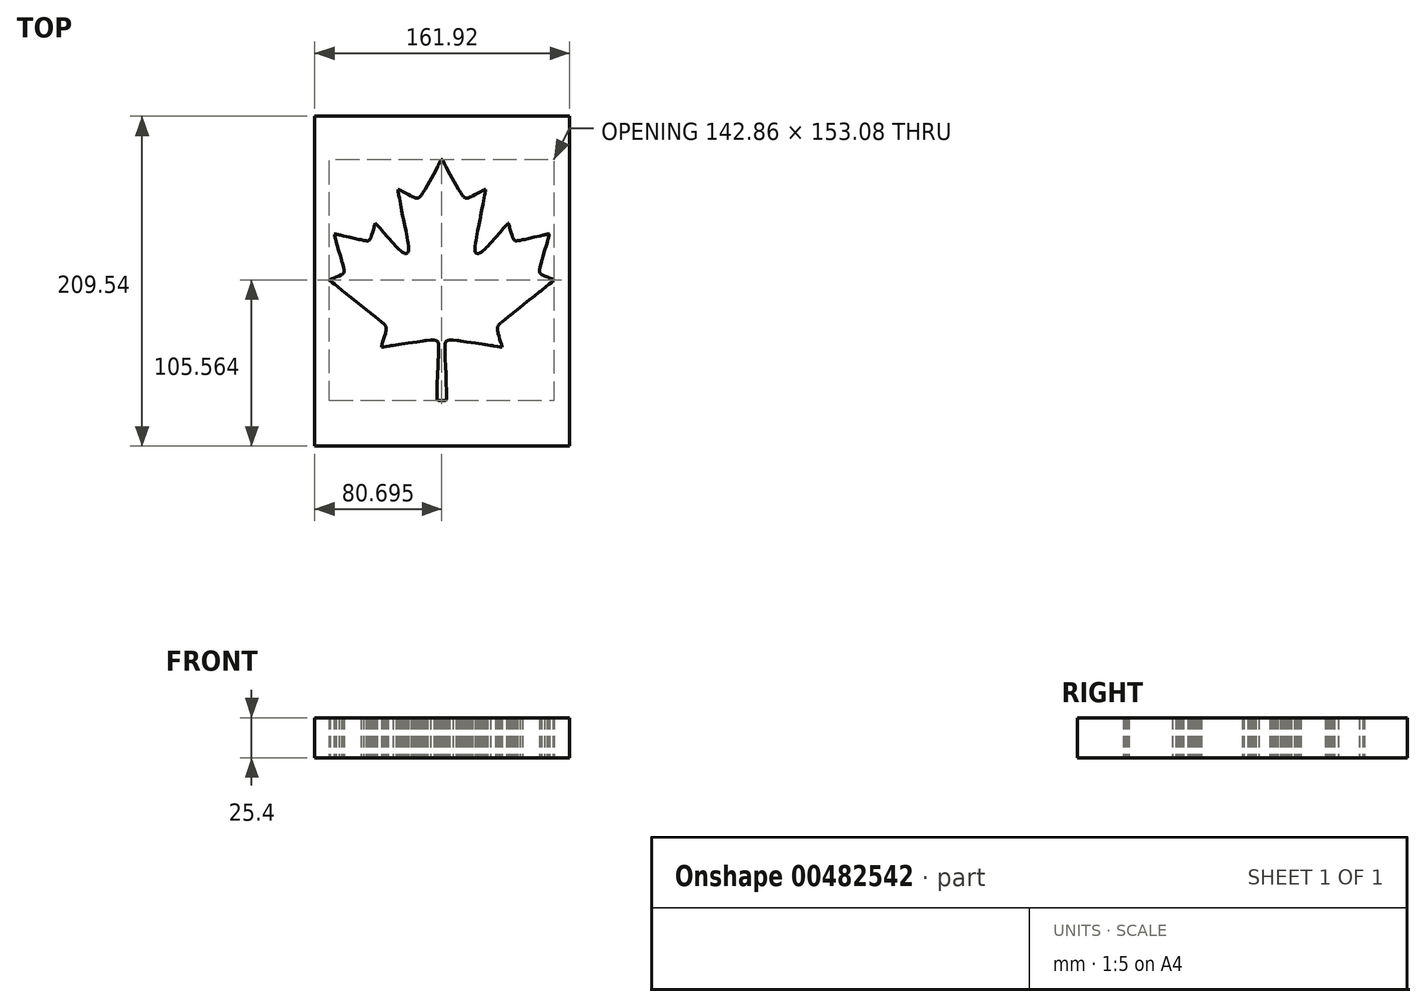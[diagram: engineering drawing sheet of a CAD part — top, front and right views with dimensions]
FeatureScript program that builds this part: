
annotation { "Feature Type Name" : "Feature", "Feature Type Description" : "" }
export const myFeature = defineFeature(function(context is Context, id is Id, definition is map)
    precondition{}
    {
        {
            var Q0;
            Q0=qCreatedBy(makeId("Top.planeOp"),FACE);
            var sketch = newSketch(context, id + "F0", { "sketchPlane" : qUnion([Q0])});
            skLineSegment(sketch, "E0", {"start": v(-80.96, -104.78) * mm, "end": v(80.96, -104.78) * mm});
            skLineSegment(sketch, "E1", {"start": v(80.96, -104.78) * mm, "end": v(80.96, 104.78) * mm});
            skLineSegment(sketch, "E2", {"start": v(80.96, 104.78) * mm, "end": v(-80.96, 104.78) * mm});
            skLineSegment(sketch, "E3", {"start": v(-80.96, 104.78) * mm, "end": v(-80.96, -104.78) * mm});
            skLineSegment(sketch, "E4", {"start": v(-2.37, 73.77) * mm, "end": v(-2.87, 72.84) * mm});
            skLineSegment(sketch, "E5", {"start": v(-2.87, 72.84) * mm, "end": v(-4.36, 70.05) * mm});
            skLineSegment(sketch, "E6", {"start": v(-4.36, 70.05) * mm, "end": v(-6.8, 65.54) * mm});
            skLineSegment(sketch, "E7", {"start": v(-6.8, 65.54) * mm, "end": v(-9.3, 61.02) * mm});
            skLineSegment(sketch, "E8", {"start": v(-9.3, 61.02) * mm, "end": v(-10.93, 58.16) * mm});
            skLineSegment(sketch, "E9", {"start": v(-10.93, 58.16) * mm, "end": v(-11.5, 57.22) * mm});
            skLineSegment(sketch, "E10", {"start": v(-11.5, 57.22) * mm, "end": v(-11.71, 56.87) * mm});
            skLineSegment(sketch, "E11", {"start": v(-11.71, 56.87) * mm, "end": v(-12.38, 55.81) * mm});
            skLineSegment(sketch, "E12", {"start": v(-12.38, 55.81) * mm, "end": v(-13.11, 54.73) * mm});
            skLineSegment(sketch, "E13", {"start": v(-13.11, 54.73) * mm, "end": v(-13.72, 53.93) * mm});
            skLineSegment(sketch, "E14", {"start": v(-13.72, 53.93) * mm, "end": v(-14.22, 53.37) * mm});
            skLineSegment(sketch, "E15", {"start": v(-14.22, 53.37) * mm, "end": v(-14.64, 53) * mm});
            skLineSegment(sketch, "E16", {"start": v(-14.64, 53) * mm, "end": v(-15, 52.8) * mm});
            skLineSegment(sketch, "E17", {"start": v(-15, 52.8) * mm, "end": v(-15.32, 52.7) * mm});
            skLineSegment(sketch, "E18", {"start": v(-15.32, 52.7) * mm, "end": v(-15.55, 52.68) * mm});
            skLineSegment(sketch, "E19", {"start": v(-15.55, 52.68) * mm, "end": v(-15.63, 52.68) * mm});
            skLineSegment(sketch, "E20", {"start": v(-15.63, 52.68) * mm, "end": v(-15.79, 52.68) * mm});
            skLineSegment(sketch, "E21", {"start": v(-15.79, 52.68) * mm, "end": v(-16.27, 52.73) * mm});
            skLineSegment(sketch, "E22", {"start": v(-16.27, 52.73) * mm, "end": v(-17.05, 52.92) * mm});
            skLineSegment(sketch, "E23", {"start": v(-17.05, 52.92) * mm, "end": v(-18.08, 53.32) * mm});
            skLineSegment(sketch, "E24", {"start": v(-18.08, 53.32) * mm, "end": v(-19.13, 53.8) * mm});
            skLineSegment(sketch, "E25", {"start": v(-19.13, 53.8) * mm, "end": v(-19.47, 53.98) * mm});
            skLineSegment(sketch, "E26", {"start": v(-19.47, 53.98) * mm, "end": v(-19.92, 54.2) * mm});
            skLineSegment(sketch, "E27", {"start": v(-19.92, 54.2) * mm, "end": v(-21.26, 54.9) * mm});
            skLineSegment(sketch, "E28", {"start": v(-21.26, 54.9) * mm, "end": v(-23.23, 55.96) * mm});
            skLineSegment(sketch, "E29", {"start": v(-23.23, 55.96) * mm, "end": v(-25.13, 56.98) * mm});
            skLineSegment(sketch, "E30", {"start": v(-25.13, 56.98) * mm, "end": v(-26.27, 57.6) * mm});
            skLineSegment(sketch, "E31", {"start": v(-26.27, 57.6) * mm, "end": v(-26.65, 57.8) * mm});
            skLineSegment(sketch, "E32", {"start": v(-26.65, 57.8) * mm, "end": v(-26.8, 57.88) * mm});
            skLineSegment(sketch, "E33", {"start": v(-26.8, 57.88) * mm, "end": v(-27.2, 58.09) * mm});
            skLineSegment(sketch, "E34", {"start": v(-27.2, 58.09) * mm, "end": v(-27.6, 58.26) * mm});
            skLineSegment(sketch, "E35", {"start": v(-27.6, 58.26) * mm, "end": v(-27.88, 58.28) * mm});
            skLineSegment(sketch, "E36", {"start": v(-27.88, 58.28) * mm, "end": v(-28.03, 58.14) * mm});
            skLineSegment(sketch, "E37", {"start": v(-28.03, 58.14) * mm, "end": v(-28.07, 57.82) * mm});
            skLineSegment(sketch, "E38", {"start": v(-28.07, 57.82) * mm, "end": v(-28.02, 57.29) * mm});
            skLineSegment(sketch, "E39", {"start": v(-28.02, 57.29) * mm, "end": v(-27.9, 56.52) * mm});
            skLineSegment(sketch, "E40", {"start": v(-27.9, 56.52) * mm, "end": v(-27.75, 55.76) * mm});
            skLineSegment(sketch, "E41", {"start": v(-27.75, 55.76) * mm, "end": v(-27.7, 55.5) * mm});
            skLineSegment(sketch, "E42", {"start": v(-27.7, 55.5) * mm, "end": v(-27.57, 54.8) * mm});
            skLineSegment(sketch, "E43", {"start": v(-27.57, 54.8) * mm, "end": v(-27.17, 52.68) * mm});
            skLineSegment(sketch, "E44", {"start": v(-27.17, 52.68) * mm, "end": v(-26.47, 49.02) * mm});
            skLineSegment(sketch, "E45", {"start": v(-26.47, 49.02) * mm, "end": v(-25.67, 44.82) * mm});
            skLineSegment(sketch, "E46", {"start": v(-25.67, 44.82) * mm, "end": v(-25.02, 41.47) * mm});
            skLineSegment(sketch, "E47", {"start": v(-25.02, 41.47) * mm, "end": v(-24.8, 40.35) * mm});
            skLineSegment(sketch, "E48", {"start": v(-24.8, 40.35) * mm, "end": v(-24.59, 39.24) * mm});
            skLineSegment(sketch, "E49", {"start": v(-24.59, 39.24) * mm, "end": v(-23.93, 35.9) * mm});
            skLineSegment(sketch, "E50", {"start": v(-23.93, 35.9) * mm, "end": v(-23.1, 31.68) * mm});
            skLineSegment(sketch, "E51", {"start": v(-23.1, 31.68) * mm, "end": v(-22.37, 27.9) * mm});
            skLineSegment(sketch, "E52", {"start": v(-22.37, 27.9) * mm, "end": v(-21.95, 25.55) * mm});
            skLineSegment(sketch, "E53", {"start": v(-21.95, 25.55) * mm, "end": v(-21.82, 24.76) * mm});
            skLineSegment(sketch, "E54", {"start": v(-21.82, 24.76) * mm, "end": v(-21.72, 24.17) * mm});
            skLineSegment(sketch, "E55", {"start": v(-21.72, 24.17) * mm, "end": v(-21.47, 22.4) * mm});
            skLineSegment(sketch, "E56", {"start": v(-21.47, 22.4) * mm, "end": v(-21.32, 20.72) * mm});
            skLineSegment(sketch, "E57", {"start": v(-21.32, 20.72) * mm, "end": v(-21.33, 19.56) * mm});
            skLineSegment(sketch, "E58", {"start": v(-21.33, 19.56) * mm, "end": v(-21.42, 18.94) * mm});
            skLineSegment(sketch, "E59", {"start": v(-21.42, 18.94) * mm, "end": v(-21.48, 18.75) * mm});
            skLineSegment(sketch, "E60", {"start": v(-21.48, 18.75) * mm, "end": v(-21.55, 18.52) * mm});
            skLineSegment(sketch, "E61", {"start": v(-21.55, 18.52) * mm, "end": v(-22.09, 17.73) * mm});
            skLineSegment(sketch, "E62", {"start": v(-22.09, 17.73) * mm, "end": v(-22.93, 17.43) * mm});
            skLineSegment(sketch, "E63", {"start": v(-22.93, 17.43) * mm, "end": v(-23.15, 17.43) * mm});
            skLineSegment(sketch, "E64", {"start": v(-23.15, 17.43) * mm, "end": v(-23.24, 17.44) * mm});
            skLineSegment(sketch, "E65", {"start": v(-23.24, 17.44) * mm, "end": v(-23.5, 17.47) * mm});
            skLineSegment(sketch, "E66", {"start": v(-23.5, 17.47) * mm, "end": v(-23.9, 17.59) * mm});
            skLineSegment(sketch, "E67", {"start": v(-23.9, 17.59) * mm, "end": v(-24.36, 17.8) * mm});
            skLineSegment(sketch, "E68", {"start": v(-24.36, 17.8) * mm, "end": v(-24.93, 18.13) * mm});
            skLineSegment(sketch, "E69", {"start": v(-24.93, 18.13) * mm, "end": v(-25.6, 18.63) * mm});
            skLineSegment(sketch, "E70", {"start": v(-25.6, 18.63) * mm, "end": v(-26.42, 19.3) * mm});
            skLineSegment(sketch, "E71", {"start": v(-26.42, 19.3) * mm, "end": v(-27.38, 20.2) * mm});
            skLineSegment(sketch, "E72", {"start": v(-27.38, 20.2) * mm, "end": v(-28.24, 21.03) * mm});
            skLineSegment(sketch, "E73", {"start": v(-28.24, 21.03) * mm, "end": v(-28.52, 21.32) * mm});
            skLineSegment(sketch, "E74", {"start": v(-28.52, 21.32) * mm, "end": v(-29.23, 22.04) * mm});
            skLineSegment(sketch, "E75", {"start": v(-29.23, 22.04) * mm, "end": v(-31.3, 24.28) * mm});
            skLineSegment(sketch, "E76", {"start": v(-31.3, 24.28) * mm, "end": v(-34.42, 27.75) * mm});
            skLineSegment(sketch, "E77", {"start": v(-34.42, 27.75) * mm, "end": v(-37.43, 31.17) * mm});
            skLineSegment(sketch, "E78", {"start": v(-37.43, 31.17) * mm, "end": v(-39.27, 33.28) * mm});
            skLineSegment(sketch, "E79", {"start": v(-39.27, 33.28) * mm, "end": v(-39.89, 33.98) * mm});
            skLineSegment(sketch, "E80", {"start": v(-39.89, 33.98) * mm, "end": v(-40.11, 34.24) * mm});
            skLineSegment(sketch, "E81", {"start": v(-40.11, 34.24) * mm, "end": v(-40.78, 35) * mm});
            skLineSegment(sketch, "E82", {"start": v(-40.78, 35) * mm, "end": v(-41.46, 35.78) * mm});
            skLineSegment(sketch, "E83", {"start": v(-41.46, 35.78) * mm, "end": v(-41.94, 36.32) * mm});
            skLineSegment(sketch, "E84", {"start": v(-41.94, 36.32) * mm, "end": v(-42.28, 36.68) * mm});
            skLineSegment(sketch, "E85", {"start": v(-42.28, 36.68) * mm, "end": v(-42.48, 36.87) * mm});
            skLineSegment(sketch, "E86", {"start": v(-42.48, 36.87) * mm, "end": v(-42.6, 36.95) * mm});
            skLineSegment(sketch, "E87", {"start": v(-42.6, 36.95) * mm, "end": v(-42.64, 36.94) * mm});
            skLineSegment(sketch, "E88", {"start": v(-42.64, 36.94) * mm, "end": v(-42.66, 36.9) * mm});
            skLineSegment(sketch, "E89", {"start": v(-42.66, 36.9) * mm, "end": v(-42.66, 36.88) * mm});
            skLineSegment(sketch, "E90", {"start": v(-42.66, 36.88) * mm, "end": v(-42.67, 36.82) * mm});
            skLineSegment(sketch, "E91", {"start": v(-42.67, 36.82) * mm, "end": v(-42.7, 36.66) * mm});
            skLineSegment(sketch, "E92", {"start": v(-42.7, 36.66) * mm, "end": v(-42.78, 36.25) * mm});
            skLineSegment(sketch, "E93", {"start": v(-42.78, 36.25) * mm, "end": v(-42.95, 35.54) * mm});
            skLineSegment(sketch, "E94", {"start": v(-42.95, 35.54) * mm, "end": v(-43.17, 34.7) * mm});
            skLineSegment(sketch, "E95", {"start": v(-43.17, 34.7) * mm, "end": v(-43.25, 34.43) * mm});
            skLineSegment(sketch, "E96", {"start": v(-43.25, 34.43) * mm, "end": v(-43.36, 34.03) * mm});
            skLineSegment(sketch, "E97", {"start": v(-43.36, 34.03) * mm, "end": v(-43.71, 32.86) * mm});
            skLineSegment(sketch, "E98", {"start": v(-43.71, 32.86) * mm, "end": v(-44.28, 31.03) * mm});
            skLineSegment(sketch, "E99", {"start": v(-44.28, 31.03) * mm, "end": v(-44.88, 29.23) * mm});
            skLineSegment(sketch, "E100", {"start": v(-44.88, 29.23) * mm, "end": v(-45.28, 28.08) * mm});
            skLineSegment(sketch, "E101", {"start": v(-45.28, 28.08) * mm, "end": v(-45.42, 27.7) * mm});
            skLineSegment(sketch, "E102", {"start": v(-45.42, 27.7) * mm, "end": v(-45.52, 27.44) * mm});
            skLineSegment(sketch, "E103", {"start": v(-45.52, 27.44) * mm, "end": v(-45.86, 26.67) * mm});
            skLineSegment(sketch, "E104", {"start": v(-45.86, 26.67) * mm, "end": v(-46.23, 26.06) * mm});
            skLineSegment(sketch, "E105", {"start": v(-46.23, 26.06) * mm, "end": v(-46.6, 25.76) * mm});
            skLineSegment(sketch, "E106", {"start": v(-46.6, 25.76) * mm, "end": v(-46.91, 25.66) * mm});
            skLineSegment(sketch, "E107", {"start": v(-46.91, 25.66) * mm, "end": v(-47.02, 25.65) * mm});
            skLineSegment(sketch, "E108", {"start": v(-47.02, 25.65) * mm, "end": v(-47.16, 25.63) * mm});
            skLineSegment(sketch, "E109", {"start": v(-47.16, 25.63) * mm, "end": v(-47.58, 25.62) * mm});
            skLineSegment(sketch, "E110", {"start": v(-47.58, 25.62) * mm, "end": v(-48.48, 25.7) * mm});
            skLineSegment(sketch, "E111", {"start": v(-48.48, 25.7) * mm, "end": v(-49.95, 25.95) * mm});
            skLineSegment(sketch, "E112", {"start": v(-49.95, 25.95) * mm, "end": v(-51.65, 26.3) * mm});
            skLineSegment(sketch, "E113", {"start": v(-51.65, 26.3) * mm, "end": v(-52.21, 26.4) * mm});
            skLineSegment(sketch, "E114", {"start": v(-52.21, 26.4) * mm, "end": v(-53, 26.58) * mm});
            skLineSegment(sketch, "E115", {"start": v(-53, 26.58) * mm, "end": v(-55.37, 27.1) * mm});
            skLineSegment(sketch, "E116", {"start": v(-55.37, 27.1) * mm, "end": v(-58.99, 27.93) * mm});
            skLineSegment(sketch, "E117", {"start": v(-58.99, 27.93) * mm, "end": v(-62.52, 28.74) * mm});
            skLineSegment(sketch, "E118", {"start": v(-62.52, 28.74) * mm, "end": v(-64.69, 29.24) * mm});
            skLineSegment(sketch, "E119", {"start": v(-64.69, 29.24) * mm, "end": v(-65.41, 29.4) * mm});
            skLineSegment(sketch, "E120", {"start": v(-65.41, 29.4) * mm, "end": v(-65.67, 29.47) * mm});
            skLineSegment(sketch, "E121", {"start": v(-65.67, 29.47) * mm, "end": v(-66.46, 29.65) * mm});
            skLineSegment(sketch, "E122", {"start": v(-66.46, 29.65) * mm, "end": v(-67.25, 29.82) * mm});
            skLineSegment(sketch, "E123", {"start": v(-67.25, 29.82) * mm, "end": v(-67.82, 29.93) * mm});
            skLineSegment(sketch, "E124", {"start": v(-67.82, 29.93) * mm, "end": v(-68.2, 30) * mm});
            skLineSegment(sketch, "E125", {"start": v(-68.2, 30) * mm, "end": v(-68.42, 30.02) * mm});
            skLineSegment(sketch, "E126", {"start": v(-68.42, 30.02) * mm, "end": v(-68.53, 30) * mm});
            skLineSegment(sketch, "E127", {"start": v(-68.53, 30) * mm, "end": v(-68.57, 29.95) * mm});
            skLineSegment(sketch, "E128", {"start": v(-68.57, 29.95) * mm, "end": v(-68.56, 29.89) * mm});
            skLineSegment(sketch, "E129", {"start": v(-68.56, 29.89) * mm, "end": v(-68.56, 29.87) * mm});
            skLineSegment(sketch, "E130", {"start": v(-68.56, 29.87) * mm, "end": v(-68.55, 29.81) * mm});
            skLineSegment(sketch, "E131", {"start": v(-68.55, 29.81) * mm, "end": v(-68.51, 29.62) * mm});
            skLineSegment(sketch, "E132", {"start": v(-68.51, 29.62) * mm, "end": v(-68.38, 29.04) * mm});
            skLineSegment(sketch, "E133", {"start": v(-68.38, 29.04) * mm, "end": v(-68.08, 27.9) * mm});
            skLineSegment(sketch, "E134", {"start": v(-68.08, 27.9) * mm, "end": v(-67.67, 26.4) * mm});
            skLineSegment(sketch, "E135", {"start": v(-67.67, 26.4) * mm, "end": v(-67.53, 25.91) * mm});
            skLineSegment(sketch, "E136", {"start": v(-67.53, 25.91) * mm, "end": v(-67.32, 25.18) * mm});
            skLineSegment(sketch, "E137", {"start": v(-67.32, 25.18) * mm, "end": v(-66.7, 22.98) * mm});
            skLineSegment(sketch, "E138", {"start": v(-66.7, 22.98) * mm, "end": v(-65.7, 19.47) * mm});
            skLineSegment(sketch, "E139", {"start": v(-65.7, 19.47) * mm, "end": v(-64.67, 15.86) * mm});
            skLineSegment(sketch, "E140", {"start": v(-64.67, 15.86) * mm, "end": v(-63.98, 13.46) * mm});
            skLineSegment(sketch, "E141", {"start": v(-63.98, 13.46) * mm, "end": v(-63.76, 12.66) * mm});
            skLineSegment(sketch, "E142", {"start": v(-63.76, 12.66) * mm, "end": v(-63.59, 12.06) * mm});
            skLineSegment(sketch, "E143", {"start": v(-63.59, 12.06) * mm, "end": v(-63.09, 10.25) * mm});
            skLineSegment(sketch, "E144", {"start": v(-63.09, 10.25) * mm, "end": v(-62.64, 8.54) * mm});
            skLineSegment(sketch, "E145", {"start": v(-62.64, 8.54) * mm, "end": v(-62.4, 7.36) * mm});
            skLineSegment(sketch, "E146", {"start": v(-62.4, 7.36) * mm, "end": v(-62.3, 6.73) * mm});
            skLineSegment(sketch, "E147", {"start": v(-62.3, 6.73) * mm, "end": v(-62.3, 6.52) * mm});
            skLineSegment(sketch, "E148", {"start": v(-62.3, 6.52) * mm, "end": v(-62.3, 6.36) * mm});
            skLineSegment(sketch, "E149", {"start": v(-62.3, 6.36) * mm, "end": v(-62.34, 5.86) * mm});
            skLineSegment(sketch, "E150", {"start": v(-62.34, 5.86) * mm, "end": v(-62.53, 5.3) * mm});
            skLineSegment(sketch, "E151", {"start": v(-62.53, 5.3) * mm, "end": v(-62.92, 4.82) * mm});
            skLineSegment(sketch, "E152", {"start": v(-62.92, 4.82) * mm, "end": v(-63.37, 4.46) * mm});
            skLineSegment(sketch, "E153", {"start": v(-63.37, 4.46) * mm, "end": v(-63.53, 4.36) * mm});
            skLineSegment(sketch, "E154", {"start": v(-63.53, 4.36) * mm, "end": v(-63.77, 4.2) * mm});
            skLineSegment(sketch, "E155", {"start": v(-63.77, 4.2) * mm, "end": v(-65.4, 3.4) * mm});
            skLineSegment(sketch, "E156", {"start": v(-65.4, 3.4) * mm, "end": v(-67.31, 2.6) * mm});
            skLineSegment(sketch, "E157", {"start": v(-67.31, 2.6) * mm, "end": v(-67.69, 2.44) * mm});
            skLineSegment(sketch, "E158", {"start": v(-67.69, 2.44) * mm, "end": v(-67.96, 2.33) * mm});
            skLineSegment(sketch, "E159", {"start": v(-67.96, 2.33) * mm, "end": v(-68.78, 2) * mm});
            skLineSegment(sketch, "E160", {"start": v(-68.78, 2) * mm, "end": v(-69.77, 1.58) * mm});
            skLineSegment(sketch, "E161", {"start": v(-69.77, 1.58) * mm, "end": v(-70.6, 1.23) * mm});
            skLineSegment(sketch, "E162", {"start": v(-70.6, 1.23) * mm, "end": v(-71.07, 1.04) * mm});
            skLineSegment(sketch, "E163", {"start": v(-71.07, 1.04) * mm, "end": v(-71.23, 0.97) * mm});
            skLineSegment(sketch, "E164", {"start": v(-71.23, 0.97) * mm, "end": v(-71.32, 0.93) * mm});
            skLineSegment(sketch, "E165", {"start": v(-71.32, 0.93) * mm, "end": v(-71.6, 0.8) * mm});
            skLineSegment(sketch, "E166", {"start": v(-71.6, 0.8) * mm, "end": v(-71.7, 0.63) * mm});
            skLineSegment(sketch, "E167", {"start": v(-71.7, 0.63) * mm, "end": v(-71.48, 0.38) * mm});
            skLineSegment(sketch, "E168", {"start": v(-71.48, 0.38) * mm, "end": v(-71.07, 0.05) * mm});
            skLineSegment(sketch, "E169", {"start": v(-71.07, 0.05) * mm, "end": v(-70.92, -0.06) * mm});
            skLineSegment(sketch, "E170", {"start": v(-70.92, -0.06) * mm, "end": v(-70.69, -0.24) * mm});
            skLineSegment(sketch, "E171", {"start": v(-70.69, -0.24) * mm, "end": v(-69.98, -0.78) * mm});
            skLineSegment(sketch, "E172", {"start": v(-69.98, -0.78) * mm, "end": v(-68.5, -1.93) * mm});
            skLineSegment(sketch, "E173", {"start": v(-68.5, -1.93) * mm, "end": v(-66.29, -3.66) * mm});
            skLineSegment(sketch, "E174", {"start": v(-66.29, -3.66) * mm, "end": v(-63.96, -5.5) * mm});
            skLineSegment(sketch, "E175", {"start": v(-63.96, -5.5) * mm, "end": v(-63.19, -6.12) * mm});
            skLineSegment(sketch, "E176", {"start": v(-63.19, -6.12) * mm, "end": v(-62.18, -6.93) * mm});
            skLineSegment(sketch, "E177", {"start": v(-62.18, -6.93) * mm, "end": v(-59.14, -9.36) * mm});
            skLineSegment(sketch, "E178", {"start": v(-59.14, -9.36) * mm, "end": v(-54.56, -13.05) * mm});
            skLineSegment(sketch, "E179", {"start": v(-54.56, -13.05) * mm, "end": v(-49.97, -16.73) * mm});
            skLineSegment(sketch, "E180", {"start": v(-49.97, -16.73) * mm, "end": v(-46.92, -19.18) * mm});
            skLineSegment(sketch, "E181", {"start": v(-46.92, -19.18) * mm, "end": v(-45.9, -20) * mm});
            skLineSegment(sketch, "E182", {"start": v(-45.9, -20) * mm, "end": v(-45.12, -20.62) * mm});
            skLineSegment(sketch, "E183", {"start": v(-45.12, -20.62) * mm, "end": v(-42.77, -22.5) * mm});
            skLineSegment(sketch, "E184", {"start": v(-42.77, -22.5) * mm, "end": v(-40.5, -24.3) * mm});
            skLineSegment(sketch, "E185", {"start": v(-40.5, -24.3) * mm, "end": v(-38.9, -25.57) * mm});
            skLineSegment(sketch, "E186", {"start": v(-38.9, -25.57) * mm, "end": v(-38.05, -26.25) * mm});
            skLineSegment(sketch, "E187", {"start": v(-38.05, -26.25) * mm, "end": v(-37.77, -26.49) * mm});
            skLineSegment(sketch, "E188", {"start": v(-37.77, -26.49) * mm, "end": v(-37.57, -26.66) * mm});
            skLineSegment(sketch, "E189", {"start": v(-37.57, -26.66) * mm, "end": v(-36.96, -27.2) * mm});
            skLineSegment(sketch, "E190", {"start": v(-36.96, -27.2) * mm, "end": v(-36.38, -27.8) * mm});
            skLineSegment(sketch, "E191", {"start": v(-36.38, -27.8) * mm, "end": v(-36, -28.34) * mm});
            skLineSegment(sketch, "E192", {"start": v(-36, -28.34) * mm, "end": v(-35.8, -28.76) * mm});
            skLineSegment(sketch, "E193", {"start": v(-35.8, -28.76) * mm, "end": v(-35.74, -28.9) * mm});
            skLineSegment(sketch, "E194", {"start": v(-35.74, -28.9) * mm, "end": v(-35.7, -29.06) * mm});
            skLineSegment(sketch, "E195", {"start": v(-35.7, -29.06) * mm, "end": v(-35.6, -29.54) * mm});
            skLineSegment(sketch, "E196", {"start": v(-35.6, -29.54) * mm, "end": v(-35.56, -30.36) * mm});
            skLineSegment(sketch, "E197", {"start": v(-35.56, -30.36) * mm, "end": v(-35.68, -31.45) * mm});
            skLineSegment(sketch, "E198", {"start": v(-35.68, -31.45) * mm, "end": v(-35.9, -32.55) * mm});
            skLineSegment(sketch, "E199", {"start": v(-35.9, -32.55) * mm, "end": v(-36, -32.91) * mm});
            skLineSegment(sketch, "E200", {"start": v(-36, -32.91) * mm, "end": v(-36.1, -33.38) * mm});
            skLineSegment(sketch, "E201", {"start": v(-36.1, -33.38) * mm, "end": v(-36.5, -34.77) * mm});
            skLineSegment(sketch, "E202", {"start": v(-36.5, -34.77) * mm, "end": v(-37.1, -36.82) * mm});
            skLineSegment(sketch, "E203", {"start": v(-37.1, -36.82) * mm, "end": v(-37.7, -38.77) * mm});
            skLineSegment(sketch, "E204", {"start": v(-37.7, -38.77) * mm, "end": v(-38.07, -39.95) * mm});
            skLineSegment(sketch, "E205", {"start": v(-38.07, -39.95) * mm, "end": v(-38.18, -40.34) * mm});
            skLineSegment(sketch, "E206", {"start": v(-38.18, -40.34) * mm, "end": v(-38.25, -40.59) * mm});
            skLineSegment(sketch, "E207", {"start": v(-38.25, -40.59) * mm, "end": v(-38.44, -41.33) * mm});
            skLineSegment(sketch, "E208", {"start": v(-38.44, -41.33) * mm, "end": v(-38.52, -41.82) * mm});
            skLineSegment(sketch, "E209", {"start": v(-38.52, -41.82) * mm, "end": v(-38.47, -41.98) * mm});
            skLineSegment(sketch, "E210", {"start": v(-38.47, -41.98) * mm, "end": v(-38.37, -41.98) * mm});
            skLineSegment(sketch, "E211", {"start": v(-38.37, -41.98) * mm, "end": v(-38.34, -41.98) * mm});
            skLineSegment(sketch, "E212", {"start": v(-38.34, -41.98) * mm, "end": v(-38.3, -41.96) * mm});
            skLineSegment(sketch, "E213", {"start": v(-38.3, -41.96) * mm, "end": v(-38.1, -41.92) * mm});
            skLineSegment(sketch, "E214", {"start": v(-38.1, -41.92) * mm, "end": v(-37.37, -41.78) * mm});
            skLineSegment(sketch, "E215", {"start": v(-37.37, -41.78) * mm, "end": v(-35.67, -41.5) * mm});
            skLineSegment(sketch, "E216", {"start": v(-35.67, -41.5) * mm, "end": v(-33.3, -41.12) * mm});
            skLineSegment(sketch, "E217", {"start": v(-33.3, -41.12) * mm, "end": v(-32.5, -41) * mm});
            skLineSegment(sketch, "E218", {"start": v(-32.5, -41) * mm, "end": v(-31.3, -40.8) * mm});
            skLineSegment(sketch, "E219", {"start": v(-31.3, -40.8) * mm, "end": v(-27.66, -40.24) * mm});
            skLineSegment(sketch, "E220", {"start": v(-27.66, -40.24) * mm, "end": v(-21.8, -39.35) * mm});
            skLineSegment(sketch, "E221", {"start": v(-21.8, -39.35) * mm, "end": v(-15.88, -38.5) * mm});
            skLineSegment(sketch, "E222", {"start": v(-15.88, -38.5) * mm, "end": v(-12.08, -37.99) * mm});
            skLineSegment(sketch, "E223", {"start": v(-12.08, -37.99) * mm, "end": v(-10.8, -37.84) * mm});
            skLineSegment(sketch, "E224", {"start": v(-10.8, -37.84) * mm, "end": v(-9.93, -37.74) * mm});
            skLineSegment(sketch, "E225", {"start": v(-9.93, -37.74) * mm, "end": v(-7.3, -37.5) * mm});
            skLineSegment(sketch, "E226", {"start": v(-7.3, -37.5) * mm, "end": v(-5.16, -37.45) * mm});
            skLineSegment(sketch, "E227", {"start": v(-5.16, -37.45) * mm, "end": v(-3.98, -37.61) * mm});
            skLineSegment(sketch, "E228", {"start": v(-3.98, -37.61) * mm, "end": v(-3.5, -37.81) * mm});
            skLineSegment(sketch, "E229", {"start": v(-3.5, -37.81) * mm, "end": v(-3.37, -37.91) * mm});
            skLineSegment(sketch, "E230", {"start": v(-3.37, -37.91) * mm, "end": v(-3.22, -38.03) * mm});
            skLineSegment(sketch, "E231", {"start": v(-3.22, -38.03) * mm, "end": v(-2.7, -38.76) * mm});
            skLineSegment(sketch, "E232", {"start": v(-2.7, -38.76) * mm, "end": v(-2.44, -39.77) * mm});
            skLineSegment(sketch, "E233", {"start": v(-2.44, -39.77) * mm, "end": v(-2.41, -40.02) * mm});
            skLineSegment(sketch, "E234", {"start": v(-2.41, -40.02) * mm, "end": v(-2.38, -40.25) * mm});
            skLineSegment(sketch, "E235", {"start": v(-2.38, -40.25) * mm, "end": v(-2.34, -40.92) * mm});
            skLineSegment(sketch, "E236", {"start": v(-2.34, -40.92) * mm, "end": v(-2.31, -42.35) * mm});
            skLineSegment(sketch, "E237", {"start": v(-2.31, -42.35) * mm, "end": v(-2.35, -44.7) * mm});
            skLineSegment(sketch, "E238", {"start": v(-2.35, -44.7) * mm, "end": v(-2.43, -47.47) * mm});
            skLineSegment(sketch, "E239", {"start": v(-2.43, -47.47) * mm, "end": v(-2.46, -48.4) * mm});
            skLineSegment(sketch, "E240", {"start": v(-2.46, -48.4) * mm, "end": v(-2.51, -49.7) * mm});
            skLineSegment(sketch, "E241", {"start": v(-2.51, -49.7) * mm, "end": v(-2.66, -53.59) * mm});
            skLineSegment(sketch, "E242", {"start": v(-2.66, -53.59) * mm, "end": v(-2.9, -59.58) * mm});
            skLineSegment(sketch, "E243", {"start": v(-2.9, -59.58) * mm, "end": v(-3.12, -65.45) * mm});
            skLineSegment(sketch, "E244", {"start": v(-3.12, -65.45) * mm, "end": v(-3.24, -69.06) * mm});
            skLineSegment(sketch, "E245", {"start": v(-3.24, -69.06) * mm, "end": v(-3.26, -70.27) * mm});
            skLineSegment(sketch, "E246", {"start": v(-3.26, -70.27) * mm, "end": v(-3.28, -70.7) * mm});
            skLineSegment(sketch, "E247", {"start": v(-3.28, -70.7) * mm, "end": v(-3.3, -72.03) * mm});
            skLineSegment(sketch, "E248", {"start": v(-3.3, -72.03) * mm, "end": v(-3.3, -73.36) * mm});
            skLineSegment(sketch, "E249", {"start": v(-3.3, -73.36) * mm, "end": v(-3.26, -74.31) * mm});
            skLineSegment(sketch, "E250", {"start": v(-3.26, -74.31) * mm, "end": v(-3.18, -74.96) * mm});
            skLineSegment(sketch, "E251", {"start": v(-3.18, -74.96) * mm, "end": v(-3.06, -75.37) * mm});
            skLineSegment(sketch, "E252", {"start": v(-3.06, -75.37) * mm, "end": v(-2.9, -75.58) * mm});
            skLineSegment(sketch, "E253", {"start": v(-2.9, -75.58) * mm, "end": v(-2.7, -75.67) * mm});
            skLineSegment(sketch, "E254", {"start": v(-2.7, -75.67) * mm, "end": v(-2.53, -75.7) * mm});
            skLineSegment(sketch, "E255", {"start": v(-2.53, -75.7) * mm, "end": v(-2.46, -75.7) * mm});
            skLineSegment(sketch, "E256", {"start": v(-2.46, -75.7) * mm, "end": v(-2.13, -75.71) * mm});
            skLineSegment(sketch, "E257", {"start": v(-2.13, -75.71) * mm, "end": v(-0.27, -75.75) * mm});
            skLineSegment(sketch, "E258", {"start": v(-0.27, -75.75) * mm, "end": v(1.6, -75.71) * mm});
            skLineSegment(sketch, "E259", {"start": v(1.6, -75.71) * mm, "end": v(1.93, -75.7) * mm});
            skLineSegment(sketch, "E260", {"start": v(1.93, -75.7) * mm, "end": v(2, -75.7) * mm});
            skLineSegment(sketch, "E261", {"start": v(2, -75.7) * mm, "end": v(2.18, -75.67) * mm});
            skLineSegment(sketch, "E262", {"start": v(2.18, -75.67) * mm, "end": v(2.38, -75.58) * mm});
            skLineSegment(sketch, "E263", {"start": v(2.38, -75.58) * mm, "end": v(2.53, -75.37) * mm});
            skLineSegment(sketch, "E264", {"start": v(2.53, -75.37) * mm, "end": v(2.65, -74.96) * mm});
            skLineSegment(sketch, "E265", {"start": v(2.65, -74.96) * mm, "end": v(2.72, -74.31) * mm});
            skLineSegment(sketch, "E266", {"start": v(2.72, -74.31) * mm, "end": v(2.76, -73.36) * mm});
            skLineSegment(sketch, "E267", {"start": v(2.76, -73.36) * mm, "end": v(2.77, -72.03) * mm});
            skLineSegment(sketch, "E268", {"start": v(2.77, -72.03) * mm, "end": v(2.74, -70.7) * mm});
            skLineSegment(sketch, "E269", {"start": v(2.74, -70.7) * mm, "end": v(2.74, -70.27) * mm});
            skLineSegment(sketch, "E270", {"start": v(2.74, -70.27) * mm, "end": v(2.7, -69.06) * mm});
            skLineSegment(sketch, "E271", {"start": v(2.7, -69.06) * mm, "end": v(2.59, -65.45) * mm});
            skLineSegment(sketch, "E272", {"start": v(2.59, -65.45) * mm, "end": v(2.37, -59.58) * mm});
            skLineSegment(sketch, "E273", {"start": v(2.37, -59.58) * mm, "end": v(2.13, -53.59) * mm});
            skLineSegment(sketch, "E274", {"start": v(2.13, -53.59) * mm, "end": v(1.98, -49.7) * mm});
            skLineSegment(sketch, "E275", {"start": v(1.98, -49.7) * mm, "end": v(1.93, -48.4) * mm});
            skLineSegment(sketch, "E276", {"start": v(1.93, -48.4) * mm, "end": v(1.9, -47.47) * mm});
            skLineSegment(sketch, "E277", {"start": v(1.9, -47.47) * mm, "end": v(1.82, -44.7) * mm});
            skLineSegment(sketch, "E278", {"start": v(1.82, -44.7) * mm, "end": v(1.78, -42.35) * mm});
            skLineSegment(sketch, "E279", {"start": v(1.78, -42.35) * mm, "end": v(1.8, -40.92) * mm});
            skLineSegment(sketch, "E280", {"start": v(1.8, -40.92) * mm, "end": v(1.85, -40.25) * mm});
            skLineSegment(sketch, "E281", {"start": v(1.85, -40.25) * mm, "end": v(1.88, -40.02) * mm});
            skLineSegment(sketch, "E282", {"start": v(1.88, -40.02) * mm, "end": v(1.91, -39.77) * mm});
            skLineSegment(sketch, "E283", {"start": v(1.91, -39.77) * mm, "end": v(2.17, -38.76) * mm});
            skLineSegment(sketch, "E284", {"start": v(2.17, -38.76) * mm, "end": v(2.69, -38.03) * mm});
            skLineSegment(sketch, "E285", {"start": v(2.69, -38.03) * mm, "end": v(2.84, -37.91) * mm});
            skLineSegment(sketch, "E286", {"start": v(2.84, -37.91) * mm, "end": v(2.98, -37.81) * mm});
            skLineSegment(sketch, "E287", {"start": v(2.98, -37.81) * mm, "end": v(3.45, -37.61) * mm});
            skLineSegment(sketch, "E288", {"start": v(3.45, -37.61) * mm, "end": v(4.62, -37.45) * mm});
            skLineSegment(sketch, "E289", {"start": v(4.62, -37.45) * mm, "end": v(6.76, -37.5) * mm});
            skLineSegment(sketch, "E290", {"start": v(6.76, -37.5) * mm, "end": v(9.4, -37.74) * mm});
            skLineSegment(sketch, "E291", {"start": v(9.4, -37.74) * mm, "end": v(10.28, -37.84) * mm});
            skLineSegment(sketch, "E292", {"start": v(10.28, -37.84) * mm, "end": v(11.55, -37.99) * mm});
            skLineSegment(sketch, "E293", {"start": v(11.55, -37.99) * mm, "end": v(15.35, -38.5) * mm});
            skLineSegment(sketch, "E294", {"start": v(15.35, -38.5) * mm, "end": v(21.27, -39.35) * mm});
            skLineSegment(sketch, "E295", {"start": v(21.27, -39.35) * mm, "end": v(27.13, -40.24) * mm});
            skLineSegment(sketch, "E296", {"start": v(27.13, -40.24) * mm, "end": v(30.76, -40.8) * mm});
            skLineSegment(sketch, "E297", {"start": v(30.76, -40.8) * mm, "end": v(31.98, -41) * mm});
            skLineSegment(sketch, "E298", {"start": v(31.98, -41) * mm, "end": v(32.77, -41.12) * mm});
            skLineSegment(sketch, "E299", {"start": v(32.77, -41.12) * mm, "end": v(35.13, -41.5) * mm});
            skLineSegment(sketch, "E300", {"start": v(35.13, -41.5) * mm, "end": v(36.84, -41.78) * mm});
            skLineSegment(sketch, "E301", {"start": v(36.84, -41.78) * mm, "end": v(37.57, -41.92) * mm});
            skLineSegment(sketch, "E302", {"start": v(37.57, -41.92) * mm, "end": v(37.76, -41.96) * mm});
            skLineSegment(sketch, "E303", {"start": v(37.76, -41.96) * mm, "end": v(37.81, -41.98) * mm});
            skLineSegment(sketch, "E304", {"start": v(37.81, -41.98) * mm, "end": v(37.84, -41.98) * mm});
            skLineSegment(sketch, "E305", {"start": v(37.84, -41.98) * mm, "end": v(37.94, -41.98) * mm});
            skLineSegment(sketch, "E306", {"start": v(37.94, -41.98) * mm, "end": v(38, -41.82) * mm});
            skLineSegment(sketch, "E307", {"start": v(38, -41.82) * mm, "end": v(37.91, -41.33) * mm});
            skLineSegment(sketch, "E308", {"start": v(37.91, -41.33) * mm, "end": v(37.72, -40.59) * mm});
            skLineSegment(sketch, "E309", {"start": v(37.72, -40.59) * mm, "end": v(37.65, -40.34) * mm});
            skLineSegment(sketch, "E310", {"start": v(37.65, -40.34) * mm, "end": v(37.54, -39.95) * mm});
            skLineSegment(sketch, "E311", {"start": v(37.54, -39.95) * mm, "end": v(37.18, -38.77) * mm});
            skLineSegment(sketch, "E312", {"start": v(37.18, -38.77) * mm, "end": v(36.58, -36.82) * mm});
            skLineSegment(sketch, "E313", {"start": v(36.58, -36.82) * mm, "end": v(35.97, -34.77) * mm});
            skLineSegment(sketch, "E314", {"start": v(35.97, -34.77) * mm, "end": v(35.58, -33.38) * mm});
            skLineSegment(sketch, "E315", {"start": v(35.58, -33.38) * mm, "end": v(35.46, -32.91) * mm});
            skLineSegment(sketch, "E316", {"start": v(35.46, -32.91) * mm, "end": v(35.37, -32.55) * mm});
            skLineSegment(sketch, "E317", {"start": v(35.37, -32.55) * mm, "end": v(35.15, -31.45) * mm});
            skLineSegment(sketch, "E318", {"start": v(35.15, -31.45) * mm, "end": v(35.03, -30.36) * mm});
            skLineSegment(sketch, "E319", {"start": v(35.03, -30.36) * mm, "end": v(35.06, -29.54) * mm});
            skLineSegment(sketch, "E320", {"start": v(35.06, -29.54) * mm, "end": v(35.16, -29.06) * mm});
            skLineSegment(sketch, "E321", {"start": v(35.16, -29.06) * mm, "end": v(35.21, -28.9) * mm});
            skLineSegment(sketch, "E322", {"start": v(35.21, -28.9) * mm, "end": v(35.26, -28.76) * mm});
            skLineSegment(sketch, "E323", {"start": v(35.26, -28.76) * mm, "end": v(35.47, -28.34) * mm});
            skLineSegment(sketch, "E324", {"start": v(35.47, -28.34) * mm, "end": v(35.85, -27.8) * mm});
            skLineSegment(sketch, "E325", {"start": v(35.85, -27.8) * mm, "end": v(36.43, -27.2) * mm});
            skLineSegment(sketch, "E326", {"start": v(36.43, -27.2) * mm, "end": v(37.04, -26.66) * mm});
            skLineSegment(sketch, "E327", {"start": v(37.04, -26.66) * mm, "end": v(37.24, -26.49) * mm});
            skLineSegment(sketch, "E328", {"start": v(37.24, -26.49) * mm, "end": v(37.52, -26.25) * mm});
            skLineSegment(sketch, "E329", {"start": v(37.52, -26.25) * mm, "end": v(38.36, -25.57) * mm});
            skLineSegment(sketch, "E330", {"start": v(38.36, -25.57) * mm, "end": v(39.96, -24.3) * mm});
            skLineSegment(sketch, "E331", {"start": v(39.96, -24.3) * mm, "end": v(42.24, -22.5) * mm});
            skLineSegment(sketch, "E332", {"start": v(42.24, -22.5) * mm, "end": v(44.59, -20.62) * mm});
            skLineSegment(sketch, "E333", {"start": v(44.59, -20.62) * mm, "end": v(45.37, -20) * mm});
            skLineSegment(sketch, "E334", {"start": v(45.37, -20) * mm, "end": v(46.39, -19.18) * mm});
            skLineSegment(sketch, "E335", {"start": v(46.39, -19.18) * mm, "end": v(49.44, -16.73) * mm});
            skLineSegment(sketch, "E336", {"start": v(49.44, -16.73) * mm, "end": v(54.03, -13.05) * mm});
            skLineSegment(sketch, "E337", {"start": v(54.03, -13.05) * mm, "end": v(58.61, -9.36) * mm});
            skLineSegment(sketch, "E338", {"start": v(58.61, -9.36) * mm, "end": v(61.65, -6.93) * mm});
            skLineSegment(sketch, "E339", {"start": v(61.65, -6.93) * mm, "end": v(62.66, -6.12) * mm});
            skLineSegment(sketch, "E340", {"start": v(62.66, -6.12) * mm, "end": v(63.43, -5.5) * mm});
            skLineSegment(sketch, "E341", {"start": v(63.43, -5.5) * mm, "end": v(65.76, -3.66) * mm});
            skLineSegment(sketch, "E342", {"start": v(65.76, -3.66) * mm, "end": v(67.96, -1.93) * mm});
            skLineSegment(sketch, "E343", {"start": v(67.96, -1.93) * mm, "end": v(69.45, -0.78) * mm});
            skLineSegment(sketch, "E344", {"start": v(69.45, -0.78) * mm, "end": v(70.16, -0.24) * mm});
            skLineSegment(sketch, "E345", {"start": v(70.16, -0.24) * mm, "end": v(70.4, -0.06) * mm});
            skLineSegment(sketch, "E346", {"start": v(70.4, -0.06) * mm, "end": v(70.53, 0.05) * mm});
            skLineSegment(sketch, "E347", {"start": v(70.53, 0.05) * mm, "end": v(70.95, 0.38) * mm});
            skLineSegment(sketch, "E348", {"start": v(70.95, 0.38) * mm, "end": v(71.17, 0.63) * mm});
            skLineSegment(sketch, "E349", {"start": v(71.17, 0.63) * mm, "end": v(71.07, 0.8) * mm});
            skLineSegment(sketch, "E350", {"start": v(71.07, 0.8) * mm, "end": v(70.8, 0.93) * mm});
            skLineSegment(sketch, "E351", {"start": v(70.8, 0.93) * mm, "end": v(70.7, 0.97) * mm});
            skLineSegment(sketch, "E352", {"start": v(70.7, 0.97) * mm, "end": v(70.54, 1.04) * mm});
            skLineSegment(sketch, "E353", {"start": v(70.54, 1.04) * mm, "end": v(70.07, 1.23) * mm});
            skLineSegment(sketch, "E354", {"start": v(70.07, 1.23) * mm, "end": v(69.24, 1.58) * mm});
            skLineSegment(sketch, "E355", {"start": v(69.24, 1.58) * mm, "end": v(68.25, 2) * mm});
            skLineSegment(sketch, "E356", {"start": v(68.25, 2) * mm, "end": v(67.43, 2.33) * mm});
            skLineSegment(sketch, "E357", {"start": v(67.43, 2.33) * mm, "end": v(67.16, 2.44) * mm});
            skLineSegment(sketch, "E358", {"start": v(67.16, 2.44) * mm, "end": v(66.78, 2.6) * mm});
            skLineSegment(sketch, "E359", {"start": v(66.78, 2.6) * mm, "end": v(64.88, 3.4) * mm});
            skLineSegment(sketch, "E360", {"start": v(64.88, 3.4) * mm, "end": v(63.24, 4.2) * mm});
            skLineSegment(sketch, "E361", {"start": v(63.24, 4.2) * mm, "end": v(63, 4.36) * mm});
            skLineSegment(sketch, "E362", {"start": v(63, 4.36) * mm, "end": v(62.84, 4.46) * mm});
            skLineSegment(sketch, "E363", {"start": v(62.84, 4.46) * mm, "end": v(62.39, 4.82) * mm});
            skLineSegment(sketch, "E364", {"start": v(62.39, 4.82) * mm, "end": v(62, 5.3) * mm});
            skLineSegment(sketch, "E365", {"start": v(62, 5.3) * mm, "end": v(61.8, 5.86) * mm});
            skLineSegment(sketch, "E366", {"start": v(61.8, 5.86) * mm, "end": v(61.76, 6.36) * mm});
            skLineSegment(sketch, "E367", {"start": v(61.76, 6.36) * mm, "end": v(61.77, 6.52) * mm});
            skLineSegment(sketch, "E368", {"start": v(61.77, 6.52) * mm, "end": v(61.78, 6.73) * mm});
            skLineSegment(sketch, "E369", {"start": v(61.78, 6.73) * mm, "end": v(61.86, 7.36) * mm});
            skLineSegment(sketch, "E370", {"start": v(61.86, 7.36) * mm, "end": v(62.11, 8.54) * mm});
            skLineSegment(sketch, "E371", {"start": v(62.11, 8.54) * mm, "end": v(62.55, 10.25) * mm});
            skLineSegment(sketch, "E372", {"start": v(62.55, 10.25) * mm, "end": v(63.06, 12.06) * mm});
            skLineSegment(sketch, "E373", {"start": v(63.06, 12.06) * mm, "end": v(63.23, 12.66) * mm});
            skLineSegment(sketch, "E374", {"start": v(63.23, 12.66) * mm, "end": v(63.45, 13.46) * mm});
            skLineSegment(sketch, "E375", {"start": v(63.45, 13.46) * mm, "end": v(64.14, 15.86) * mm});
            skLineSegment(sketch, "E376", {"start": v(64.14, 15.86) * mm, "end": v(65.17, 19.47) * mm});
            skLineSegment(sketch, "E377", {"start": v(65.17, 19.47) * mm, "end": v(66.17, 22.98) * mm});
            skLineSegment(sketch, "E378", {"start": v(66.17, 22.98) * mm, "end": v(66.8, 25.18) * mm});
            skLineSegment(sketch, "E379", {"start": v(66.8, 25.18) * mm, "end": v(67, 25.91) * mm});
            skLineSegment(sketch, "E380", {"start": v(67, 25.91) * mm, "end": v(67.14, 26.4) * mm});
            skLineSegment(sketch, "E381", {"start": v(67.14, 26.4) * mm, "end": v(67.54, 27.9) * mm});
            skLineSegment(sketch, "E382", {"start": v(67.54, 27.9) * mm, "end": v(67.85, 29.04) * mm});
            skLineSegment(sketch, "E383", {"start": v(67.85, 29.04) * mm, "end": v(67.98, 29.62) * mm});
            skLineSegment(sketch, "E384", {"start": v(67.98, 29.62) * mm, "end": v(68.02, 29.81) * mm});
            skLineSegment(sketch, "E385", {"start": v(68.02, 29.81) * mm, "end": v(68.03, 29.87) * mm});
            skLineSegment(sketch, "E386", {"start": v(68.03, 29.87) * mm, "end": v(68.03, 29.89) * mm});
            skLineSegment(sketch, "E387", {"start": v(68.03, 29.89) * mm, "end": v(68.04, 29.95) * mm});
            skLineSegment(sketch, "E388", {"start": v(68.04, 29.95) * mm, "end": v(68, 30) * mm});
            skLineSegment(sketch, "E389", {"start": v(68, 30) * mm, "end": v(67.89, 30.02) * mm});
            skLineSegment(sketch, "E390", {"start": v(67.89, 30.02) * mm, "end": v(67.66, 30) * mm});
            skLineSegment(sketch, "E391", {"start": v(67.66, 30) * mm, "end": v(67.29, 29.93) * mm});
            skLineSegment(sketch, "E392", {"start": v(67.29, 29.93) * mm, "end": v(66.72, 29.82) * mm});
            skLineSegment(sketch, "E393", {"start": v(66.72, 29.82) * mm, "end": v(65.93, 29.65) * mm});
            skLineSegment(sketch, "E394", {"start": v(65.93, 29.65) * mm, "end": v(65.14, 29.47) * mm});
            skLineSegment(sketch, "E395", {"start": v(65.14, 29.47) * mm, "end": v(64.88, 29.4) * mm});
            skLineSegment(sketch, "E396", {"start": v(64.88, 29.4) * mm, "end": v(64.16, 29.24) * mm});
            skLineSegment(sketch, "E397", {"start": v(64.16, 29.24) * mm, "end": v(61.99, 28.74) * mm});
            skLineSegment(sketch, "E398", {"start": v(61.99, 28.74) * mm, "end": v(58.46, 27.93) * mm});
            skLineSegment(sketch, "E399", {"start": v(58.46, 27.93) * mm, "end": v(54.84, 27.1) * mm});
            skLineSegment(sketch, "E400", {"start": v(54.84, 27.1) * mm, "end": v(52.47, 26.58) * mm});
            skLineSegment(sketch, "E401", {"start": v(52.47, 26.58) * mm, "end": v(51.68, 26.4) * mm});
            skLineSegment(sketch, "E402", {"start": v(51.68, 26.4) * mm, "end": v(51.12, 26.3) * mm});
            skLineSegment(sketch, "E403", {"start": v(51.12, 26.3) * mm, "end": v(49.42, 25.95) * mm});
            skLineSegment(sketch, "E404", {"start": v(49.42, 25.95) * mm, "end": v(47.95, 25.7) * mm});
            skLineSegment(sketch, "E405", {"start": v(47.95, 25.7) * mm, "end": v(47.05, 25.62) * mm});
            skLineSegment(sketch, "E406", {"start": v(47.05, 25.62) * mm, "end": v(46.63, 25.63) * mm});
            skLineSegment(sketch, "E407", {"start": v(46.63, 25.63) * mm, "end": v(46.5, 25.65) * mm});
            skLineSegment(sketch, "E408", {"start": v(46.5, 25.65) * mm, "end": v(46.38, 25.66) * mm});
            skLineSegment(sketch, "E409", {"start": v(46.38, 25.66) * mm, "end": v(46.07, 25.76) * mm});
            skLineSegment(sketch, "E410", {"start": v(46.07, 25.76) * mm, "end": v(45.7, 26.06) * mm});
            skLineSegment(sketch, "E411", {"start": v(45.7, 26.06) * mm, "end": v(45.33, 26.67) * mm});
            skLineSegment(sketch, "E412", {"start": v(45.33, 26.67) * mm, "end": v(44.99, 27.44) * mm});
            skLineSegment(sketch, "E413", {"start": v(44.99, 27.44) * mm, "end": v(44.89, 27.7) * mm});
            skLineSegment(sketch, "E414", {"start": v(44.89, 27.7) * mm, "end": v(44.74, 28.08) * mm});
            skLineSegment(sketch, "E415", {"start": v(44.74, 28.08) * mm, "end": v(44.35, 29.23) * mm});
            skLineSegment(sketch, "E416", {"start": v(44.35, 29.23) * mm, "end": v(43.75, 31.03) * mm});
            skLineSegment(sketch, "E417", {"start": v(43.75, 31.03) * mm, "end": v(43.18, 32.86) * mm});
            skLineSegment(sketch, "E418", {"start": v(43.18, 32.86) * mm, "end": v(42.83, 34.03) * mm});
            skLineSegment(sketch, "E419", {"start": v(42.83, 34.03) * mm, "end": v(42.72, 34.43) * mm});
            skLineSegment(sketch, "E420", {"start": v(42.72, 34.43) * mm, "end": v(42.64, 34.7) * mm});
            skLineSegment(sketch, "E421", {"start": v(42.64, 34.7) * mm, "end": v(42.41, 35.54) * mm});
            skLineSegment(sketch, "E422", {"start": v(42.41, 35.54) * mm, "end": v(42.25, 36.25) * mm});
            skLineSegment(sketch, "E423", {"start": v(42.25, 36.25) * mm, "end": v(42.17, 36.66) * mm});
            skLineSegment(sketch, "E424", {"start": v(42.17, 36.66) * mm, "end": v(42.14, 36.82) * mm});
            skLineSegment(sketch, "E425", {"start": v(42.14, 36.82) * mm, "end": v(42.13, 36.88) * mm});
            skLineSegment(sketch, "E426", {"start": v(42.13, 36.88) * mm, "end": v(42.13, 36.9) * mm});
            skLineSegment(sketch, "E427", {"start": v(42.13, 36.9) * mm, "end": v(42.11, 36.94) * mm});
            skLineSegment(sketch, "E428", {"start": v(42.11, 36.94) * mm, "end": v(42.06, 36.95) * mm});
            skLineSegment(sketch, "E429", {"start": v(42.06, 36.95) * mm, "end": v(41.95, 36.87) * mm});
            skLineSegment(sketch, "E430", {"start": v(41.95, 36.87) * mm, "end": v(41.75, 36.68) * mm});
            skLineSegment(sketch, "E431", {"start": v(41.75, 36.68) * mm, "end": v(41.41, 36.32) * mm});
            skLineSegment(sketch, "E432", {"start": v(41.41, 36.32) * mm, "end": v(40.93, 35.78) * mm});
            skLineSegment(sketch, "E433", {"start": v(40.93, 35.78) * mm, "end": v(40.25, 35) * mm});
            skLineSegment(sketch, "E434", {"start": v(40.25, 35) * mm, "end": v(39.58, 34.24) * mm});
            skLineSegment(sketch, "E435", {"start": v(39.58, 34.24) * mm, "end": v(39.36, 33.98) * mm});
            skLineSegment(sketch, "E436", {"start": v(39.36, 33.98) * mm, "end": v(38.74, 33.28) * mm});
            skLineSegment(sketch, "E437", {"start": v(38.74, 33.28) * mm, "end": v(36.9, 31.17) * mm});
            skLineSegment(sketch, "E438", {"start": v(36.9, 31.17) * mm, "end": v(33.9, 27.75) * mm});
            skLineSegment(sketch, "E439", {"start": v(33.9, 27.75) * mm, "end": v(30.78, 24.28) * mm});
            skLineSegment(sketch, "E440", {"start": v(30.78, 24.28) * mm, "end": v(28.7, 22.04) * mm});
            skLineSegment(sketch, "E441", {"start": v(28.7, 22.04) * mm, "end": v(28, 21.32) * mm});
            skLineSegment(sketch, "E442", {"start": v(28, 21.32) * mm, "end": v(27.71, 21.03) * mm});
            skLineSegment(sketch, "E443", {"start": v(27.71, 21.03) * mm, "end": v(26.85, 20.2) * mm});
            skLineSegment(sketch, "E444", {"start": v(26.85, 20.2) * mm, "end": v(25.89, 19.3) * mm});
            skLineSegment(sketch, "E445", {"start": v(25.89, 19.3) * mm, "end": v(25.08, 18.63) * mm});
            skLineSegment(sketch, "E446", {"start": v(25.08, 18.63) * mm, "end": v(24.4, 18.13) * mm});
            skLineSegment(sketch, "E447", {"start": v(24.4, 18.13) * mm, "end": v(23.83, 17.8) * mm});
            skLineSegment(sketch, "E448", {"start": v(23.83, 17.8) * mm, "end": v(23.36, 17.59) * mm});
            skLineSegment(sketch, "E449", {"start": v(23.36, 17.59) * mm, "end": v(22.97, 17.47) * mm});
            skLineSegment(sketch, "E450", {"start": v(22.97, 17.47) * mm, "end": v(22.7, 17.44) * mm});
            skLineSegment(sketch, "E451", {"start": v(22.7, 17.44) * mm, "end": v(22.62, 17.43) * mm});
            skLineSegment(sketch, "E452", {"start": v(22.62, 17.43) * mm, "end": v(22.4, 17.43) * mm});
            skLineSegment(sketch, "E453", {"start": v(22.4, 17.43) * mm, "end": v(21.56, 17.73) * mm});
            skLineSegment(sketch, "E454", {"start": v(21.56, 17.73) * mm, "end": v(21.01, 18.52) * mm});
            skLineSegment(sketch, "E455", {"start": v(21.01, 18.52) * mm, "end": v(20.95, 18.75) * mm});
            skLineSegment(sketch, "E456", {"start": v(20.95, 18.75) * mm, "end": v(20.9, 18.94) * mm});
            skLineSegment(sketch, "E457", {"start": v(20.9, 18.94) * mm, "end": v(20.8, 19.56) * mm});
            skLineSegment(sketch, "E458", {"start": v(20.8, 19.56) * mm, "end": v(20.8, 20.72) * mm});
            skLineSegment(sketch, "E459", {"start": v(20.8, 20.72) * mm, "end": v(20.94, 22.4) * mm});
            skLineSegment(sketch, "E460", {"start": v(20.94, 22.4) * mm, "end": v(21.19, 24.17) * mm});
            skLineSegment(sketch, "E461", {"start": v(21.19, 24.17) * mm, "end": v(21.29, 24.76) * mm});
            skLineSegment(sketch, "E462", {"start": v(21.29, 24.76) * mm, "end": v(21.42, 25.55) * mm});
            skLineSegment(sketch, "E463", {"start": v(21.42, 25.55) * mm, "end": v(21.84, 27.9) * mm});
            skLineSegment(sketch, "E464", {"start": v(21.84, 27.9) * mm, "end": v(22.57, 31.68) * mm});
            skLineSegment(sketch, "E465", {"start": v(22.57, 31.68) * mm, "end": v(23.4, 35.9) * mm});
            skLineSegment(sketch, "E466", {"start": v(23.4, 35.9) * mm, "end": v(24.06, 39.24) * mm});
            skLineSegment(sketch, "E467", {"start": v(24.06, 39.24) * mm, "end": v(24.28, 40.35) * mm});
            skLineSegment(sketch, "E468", {"start": v(24.28, 40.35) * mm, "end": v(24.5, 41.47) * mm});
            skLineSegment(sketch, "E469", {"start": v(24.5, 41.47) * mm, "end": v(25.14, 44.82) * mm});
            skLineSegment(sketch, "E470", {"start": v(25.14, 44.82) * mm, "end": v(25.94, 49.02) * mm});
            skLineSegment(sketch, "E471", {"start": v(25.94, 49.02) * mm, "end": v(26.64, 52.68) * mm});
            skLineSegment(sketch, "E472", {"start": v(26.64, 52.68) * mm, "end": v(27.04, 54.8) * mm});
            skLineSegment(sketch, "E473", {"start": v(27.04, 54.8) * mm, "end": v(27.17, 55.5) * mm});
            skLineSegment(sketch, "E474", {"start": v(27.17, 55.5) * mm, "end": v(27.22, 55.76) * mm});
            skLineSegment(sketch, "E475", {"start": v(27.22, 55.76) * mm, "end": v(27.36, 56.52) * mm});
            skLineSegment(sketch, "E476", {"start": v(27.36, 56.52) * mm, "end": v(27.5, 57.29) * mm});
            skLineSegment(sketch, "E477", {"start": v(27.5, 57.29) * mm, "end": v(27.54, 57.82) * mm});
            skLineSegment(sketch, "E478", {"start": v(27.54, 57.82) * mm, "end": v(27.5, 58.14) * mm});
            skLineSegment(sketch, "E479", {"start": v(27.5, 58.14) * mm, "end": v(27.35, 58.28) * mm});
            skLineSegment(sketch, "E480", {"start": v(27.35, 58.28) * mm, "end": v(27.08, 58.26) * mm});
            skLineSegment(sketch, "E481", {"start": v(27.08, 58.26) * mm, "end": v(26.67, 58.09) * mm});
            skLineSegment(sketch, "E482", {"start": v(26.67, 58.09) * mm, "end": v(26.26, 57.88) * mm});
            skLineSegment(sketch, "E483", {"start": v(26.26, 57.88) * mm, "end": v(26.12, 57.8) * mm});
            skLineSegment(sketch, "E484", {"start": v(26.12, 57.8) * mm, "end": v(25.74, 57.6) * mm});
            skLineSegment(sketch, "E485", {"start": v(25.74, 57.6) * mm, "end": v(24.6, 56.98) * mm});
            skLineSegment(sketch, "E486", {"start": v(24.6, 56.98) * mm, "end": v(22.7, 55.96) * mm});
            skLineSegment(sketch, "E487", {"start": v(22.7, 55.96) * mm, "end": v(20.73, 54.9) * mm});
            skLineSegment(sketch, "E488", {"start": v(20.73, 54.9) * mm, "end": v(19.39, 54.2) * mm});
            skLineSegment(sketch, "E489", {"start": v(19.39, 54.2) * mm, "end": v(18.94, 53.98) * mm});
            skLineSegment(sketch, "E490", {"start": v(18.94, 53.98) * mm, "end": v(18.6, 53.8) * mm});
            skLineSegment(sketch, "E491", {"start": v(18.6, 53.8) * mm, "end": v(17.55, 53.32) * mm});
            skLineSegment(sketch, "E492", {"start": v(17.55, 53.32) * mm, "end": v(16.52, 52.92) * mm});
            skLineSegment(sketch, "E493", {"start": v(16.52, 52.92) * mm, "end": v(15.74, 52.73) * mm});
            skLineSegment(sketch, "E494", {"start": v(15.74, 52.73) * mm, "end": v(15.26, 52.68) * mm});
            skLineSegment(sketch, "E495", {"start": v(15.26, 52.68) * mm, "end": v(15.1, 52.68) * mm});
            skLineSegment(sketch, "E496", {"start": v(15.1, 52.68) * mm, "end": v(15.02, 52.68) * mm});
            skLineSegment(sketch, "E497", {"start": v(15.02, 52.68) * mm, "end": v(14.8, 52.7) * mm});
            skLineSegment(sketch, "E498", {"start": v(14.8, 52.7) * mm, "end": v(14.47, 52.8) * mm});
            skLineSegment(sketch, "E499", {"start": v(14.47, 52.8) * mm, "end": v(14.1, 53) * mm});
            skLineSegment(sketch, "E500", {"start": v(14.1, 53) * mm, "end": v(13.69, 53.37) * mm});
            skLineSegment(sketch, "E501", {"start": v(13.69, 53.37) * mm, "end": v(13.19, 53.93) * mm});
            skLineSegment(sketch, "E502", {"start": v(13.19, 53.93) * mm, "end": v(12.58, 54.73) * mm});
            skLineSegment(sketch, "E503", {"start": v(12.58, 54.73) * mm, "end": v(11.85, 55.81) * mm});
            skLineSegment(sketch, "E504", {"start": v(11.85, 55.81) * mm, "end": v(11.18, 56.87) * mm});
            skLineSegment(sketch, "E505", {"start": v(11.18, 56.87) * mm, "end": v(10.97, 57.22) * mm});
            skLineSegment(sketch, "E506", {"start": v(10.97, 57.22) * mm, "end": v(10.4, 58.16) * mm});
            skLineSegment(sketch, "E507", {"start": v(10.4, 58.16) * mm, "end": v(8.77, 61.02) * mm});
            skLineSegment(sketch, "E508", {"start": v(8.77, 61.02) * mm, "end": v(6.27, 65.54) * mm});
            skLineSegment(sketch, "E509", {"start": v(6.27, 65.54) * mm, "end": v(3.83, 70.05) * mm});
            skLineSegment(sketch, "E510", {"start": v(3.83, 70.05) * mm, "end": v(2.34, 72.84) * mm});
            skLineSegment(sketch, "E511", {"start": v(2.34, 72.84) * mm, "end": v(1.85, 73.77) * mm});
            skLineSegment(sketch, "E512", {"start": v(1.85, 73.77) * mm, "end": v(1.64, 74.16) * mm});
            skLineSegment(sketch, "E513", {"start": v(1.64, 74.16) * mm, "end": v(1.04, 75.33) * mm});
            skLineSegment(sketch, "E514", {"start": v(1.04, 75.33) * mm, "end": v(0.48, 76.44) * mm});
            skLineSegment(sketch, "E515", {"start": v(0.48, 76.44) * mm, "end": v(0.07, 77.11) * mm});
            skLineSegment(sketch, "E516", {"start": v(0.07, 77.11) * mm, "end": v(-0.26, 77.33) * mm});
            skLineSegment(sketch, "E517", {"start": v(-0.26, 77.33) * mm, "end": v(-0.6, 77.11) * mm});
            skLineSegment(sketch, "E518", {"start": v(-0.6, 77.11) * mm, "end": v(-1, 76.44) * mm});
            skLineSegment(sketch, "E519", {"start": v(-1, 76.44) * mm, "end": v(-1.57, 75.33) * mm});
            skLineSegment(sketch, "E520", {"start": v(-1.57, 75.33) * mm, "end": v(-2.17, 74.16) * mm});
            skLineSegment(sketch, "E521", {"start": v(-2.17, 74.16) * mm, "end": v(-2.37, 73.77) * mm});
            skSolve(sketch);
        }
        {
            var Q0;
            Q0 = qSketchRegion(id + "F0", true);
            extrude(context, id + "F1", {"entities" : qUnion([Q0]), "depth" : 25.4 * mm});
        }
    });
